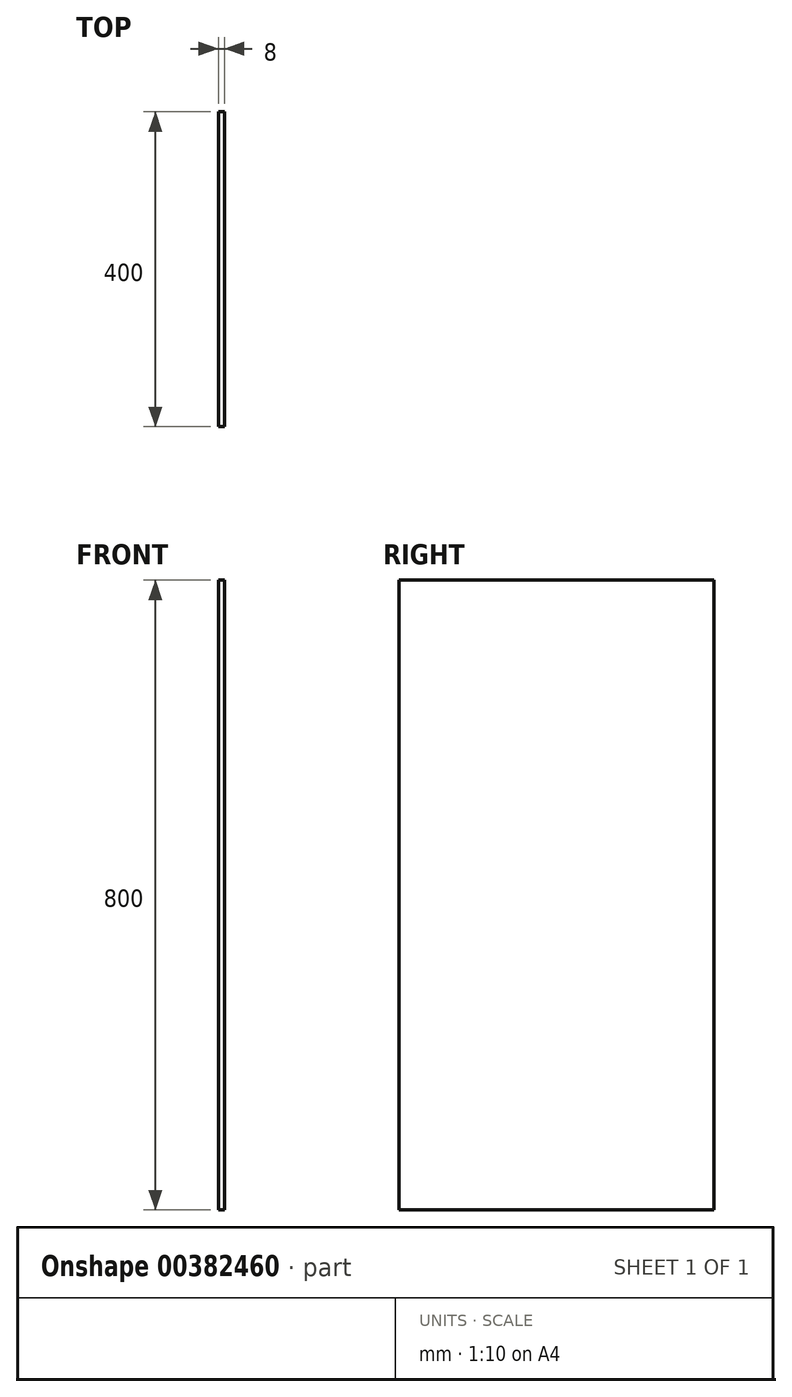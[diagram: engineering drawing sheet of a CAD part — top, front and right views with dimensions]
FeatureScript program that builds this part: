
annotation { "Feature Type Name" : "Feature", "Feature Type Description" : "" }
export const myFeature = defineFeature(function(context is Context, id is Id, definition is map)
    precondition{}
    {
        {
            var Q0;
            Q0=qCreatedBy(makeId("Right.planeOp"),FACE);
            var sketch = newSketch(context, id + "F0", { "sketchPlane" : qUnion([Q0])});
            skLineSegment(sketch, "E0.bottom", {"start": v(-200, 400) * mm, "end": v(200, 400) * mm});
            skLineSegment(sketch, "E0.top", {"start": v(-200, -400) * mm, "end": v(200, -400) * mm});
            skLineSegment(sketch, "E0.left", {"start": v(-200, 400) * mm, "end": v(-200, -400) * mm});
            skLineSegment(sketch, "E0.right", {"start": v(200, 400) * mm, "end": v(200, -400) * mm});
            skPoint(sketch, "E0.middle", {"position": v(0, 0) * mm});
            skSolve(sketch);
        }
        {
            var Q0;
            Q0=makeQuery(id+"F0.imprint","IMPRINT",FACE,{"disambiguationData":[TD([[makeQuery(id+"F0.imprint","IMPRINT",EDGE,{"derivedFrom":sQuery(id+"F0.wireOp",EDGE,"E0.bottom")}),-1.0]])]});
            extrude(context, id + "F1", {"entities" : qUnion([Q0]), "endBound" : BoundingType.SYMMETRIC, "depth" : 8 * mm});
        }
    });
